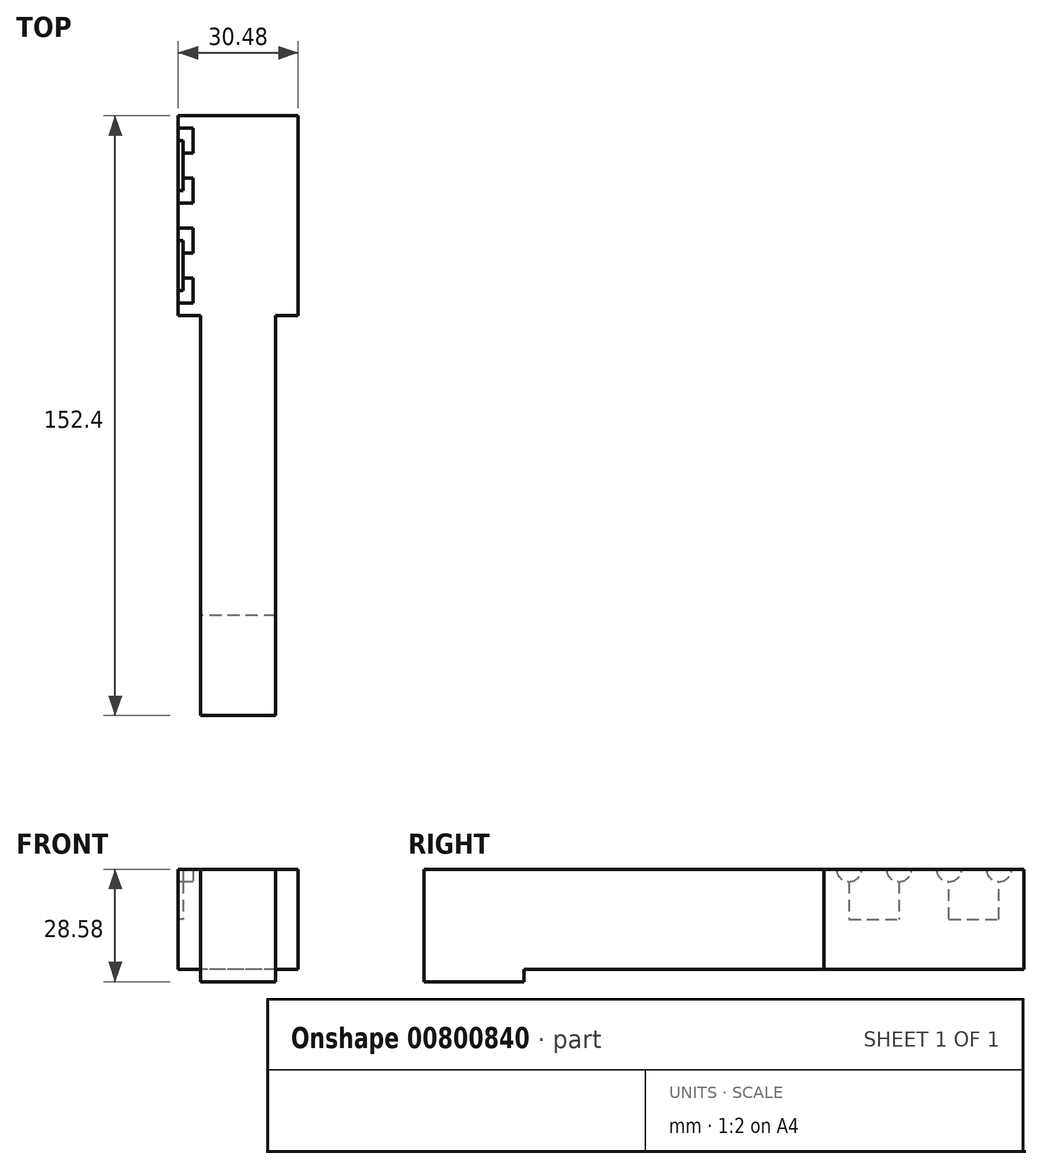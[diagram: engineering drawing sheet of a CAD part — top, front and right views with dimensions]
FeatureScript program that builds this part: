
annotation { "Feature Type Name" : "Feature", "Feature Type Description" : "" }
export const myFeature = defineFeature(function(context is Context, id is Id, definition is map)
    precondition{}
    {
        {
            var Q0;
            Q0=qCreatedBy(makeId("Right.planeOp"),FACE);
            var sketch = newSketch(context, id + "F0", { "sketchPlane" : qUnion([Q0])});
            skLineSegment(sketch, "E0", {"start": v(0, 0) * mm, "end": v(50.8, 0) * mm});
            skLineSegment(sketch, "E1", {"start": v(0, 0) * mm, "end": v(-76.2, 0) * mm});
            skLineSegment(sketch, "E2", {"start": v(50.8, 0) * mm, "end": v(50.8, 25.4) * mm});
            skLineSegment(sketch, "E3", {"start": v(50.8, 25.4) * mm, "end": v(0, 25.4) * mm});
            skLineSegment(sketch, "E4", {"start": v(0, 25.4) * mm, "end": v(0, 0) * mm});
            skLineSegment(sketch, "E5", {"start": v(-76.2, 0) * mm, "end": v(-76.2, 31.75) * mm});
            skLineSegment(sketch, "E6", {"start": v(0, 25.4) * mm, "end": v(-76.2, 25.4) * mm});
            skLineSegment(sketch, "E7", {"start": v(-76.2, 25.4) * mm, "end": v(-101.6, 25.4) * mm});
            skLineSegment(sketch, "E8", {"start": v(-101.6, 25.4) * mm, "end": v(-101.6, -3.18) * mm});
            skLineSegment(sketch, "E9", {"start": v(-101.6, -3.18) * mm, "end": v(-76.2, -3.18) * mm});
            skLineSegment(sketch, "E10", {"start": v(-76.2, -3.18) * mm, "end": v(-76.2, 0) * mm});
            skSolve(sketch);
        }
        {
            var Q0;
            {var subQ0=sQuery(id+"F0.wireOp",EDGE,"E1");Q0=makeQuery(id+"F0.imprint","IMPRINT",FACE,{"disambiguationData":[TD([[makeQuery(id+"F0.imprint","IMPRINT",EDGE,{"derivedFrom":subQ0}),-1.0]])]});}
            var Q1;
            {var subQ0=sQuery(id+"F0.wireOp",EDGE,"E7");Q1=makeQuery(id+"F0.imprint","IMPRINT",FACE,{"disambiguationData":[TD([[makeQuery(id+"F0.imprint","IMPRINT",EDGE,{"derivedFrom":subQ0}),1.0]])]});}
            extrude(context, id + "F1", {"entities" : qUnion([Q0, Q1]), "depth" : 9.52 * mm, "offsetDistance" : 25.4 * mm});
        }
        {
            var Q0;
            Q0=makeQuery(id+"F0.imprint","IMPRINT",FACE,{"disambiguationData":[TD([[makeQuery(id+"F0.imprint","IMPRINT",EDGE,{"derivedFrom":sQuery(id+"F0.wireOp",EDGE,"E0")}),1.0]])]});
            extrude(context, id + "F2", {"entities" : qUnion([Q0]), "operationType" : NewBodyOperationType.ADD, "depth" : 15.24 * mm, "offsetDistance" : 25.4 * mm});
        }
        {
            var Q0;
            Q0=makeQuery(id+"F0.imprint","IMPRINT",FACE,{"disambiguationData":[TD([[makeQuery(id+"F0.imprint","IMPRINT",EDGE,{"derivedFrom":sQuery(id+"F0.wireOp",EDGE,"E0")}),1.0]])]});
            extrude(context, id + "F3", {"entities" : qUnion([Q0]), "operationType" : NewBodyOperationType.ADD, "depth" : -15.24 * mm, "offsetDistance" : 25.4 * mm});
        }
        {
            var Q0;
            {var subQ0=sQuery(id+"F0.wireOp",EDGE,"E1");Q0=makeQuery(id+"F0.imprint","IMPRINT",FACE,{"disambiguationData":[TD([[makeQuery(id+"F0.imprint","IMPRINT",EDGE,{"derivedFrom":subQ0}),-1.0]])]});}
            var Q1;
            {var subQ0=sQuery(id+"F0.wireOp",EDGE,"E7");Q1=makeQuery(id+"F0.imprint","IMPRINT",FACE,{"disambiguationData":[TD([[makeQuery(id+"F0.imprint","IMPRINT",EDGE,{"derivedFrom":subQ0}),1.0]])]});}
            extrude(context, id + "F4", {"entities" : qUnion([Q0, Q1]), "operationType" : NewBodyOperationType.ADD, "depth" : -9.52 * mm, "offsetDistance" : 25.4 * mm});
        }
        {
            var Q0;
            Q0=makeQuery(id+"F3.opExtrude","CAP_FACE",FACE,{"disambiguationData":[OSD([sQuery(id+"F0.wireOp",EDGE,"E0"),sQuery(id+"F0.wireOp",EDGE,"E2"),sQuery(id+"F0.wireOp",EDGE,"E3"),sQuery(id+"F0.wireOp",EDGE,"E4")])],"isStart":false});
            var sketch = newSketch(context, id + "F5", { "sketchPlane" : qUnion([Q0])});
            skLineSegment(sketch, "E11", {"start": v(0, 12.7) * mm, "end": v(-50.8, 12.7) * mm});
            skLineSegment(sketch, "E12", {"start": v(0, 12.7) * mm, "end": v(0, 6.35) * mm});
            skLineSegment(sketch, "E13", {"start": v(0, 6.35) * mm, "end": v(-50.8, 6.35) * mm});
            skLineSegment(sketch, "E14", {"start": v(-25.4, 25.4) * mm, "end": v(-25.4, 12.7) * mm});
            skLineSegment(sketch, "E15", {"start": v(0, 25.4) * mm, "end": v(-12.7, 25.4) * mm});
            skLineSegment(sketch, "E16", {"start": v(-50.8, 25.4) * mm, "end": v(-38.1, 25.4) * mm});
            skLineSegment(sketch, "E17", {"start": v(-38.1, 25.4) * mm, "end": v(-38.1, 12.7) * mm});
            skLineSegment(sketch, "E18", {"start": v(-38.1, 12.7) * mm, "end": v(-44.45, 12.7) * mm});
            skLineSegment(sketch, "E19", {"start": v(-44.45, 12.7) * mm, "end": v(-31.75, 12.7) * mm});
            skLineSegment(sketch, "E20", {"start": v(-31.75, 12.7) * mm, "end": v(-31.75, 25.4) * mm});
            skLineSegment(sketch, "E21", {"start": v(-44.45, 12.7) * mm, "end": v(-44.45, 25.4) * mm});
            skLineSegment(sketch, "E22", {"start": v(-12.7, 25.4) * mm, "end": v(-12.7, 12.7) * mm});
            skLineSegment(sketch, "E23", {"start": v(-6.35, 25.4) * mm, "end": v(-6.35, 12.7) * mm});
            skLineSegment(sketch, "E24", {"start": v(-12.7, 25.4) * mm, "end": v(-25.4, 25.4) * mm});
            skLineSegment(sketch, "E25", {"start": v(-19.05, 25.4) * mm, "end": v(-19.05, 12.7) * mm});
            skArc(sketch, "E26", {"start": v(-28.57, 25.4) * mm, "mid": v(-31.75, 22.23) * mm, "end": v(-34.92, 25.4) * mm});
            skArc(sketch, "E27", {"start": v(-41.28, 25.4) * mm, "mid": v(-44.45, 22.23) * mm, "end": v(-47.62, 25.4) * mm});
            skArc(sketch, "E28", {"start": v(-3.18, 25.4) * mm, "mid": v(-6.35, 22.23) * mm, "end": v(-9.53, 25.4) * mm});
            skArc(sketch, "E29", {"start": v(-15.88, 25.4) * mm, "mid": v(-19.05, 22.23) * mm, "end": v(-22.23, 25.4) * mm});
            skLineSegment(sketch, "E30", {"start": v(-44.45, 12.7) * mm, "end": v(-47.62, 12.7) * mm});
            skLineSegment(sketch, "E31", {"start": v(-47.62, 12.7) * mm, "end": v(-47.62, 6.35) * mm});
            skLineSegment(sketch, "E32", {"start": v(-25.4, 12.7) * mm, "end": v(-25.4, 6.35) * mm});
            skLineSegment(sketch, "E33", {"start": v(-6.35, 12.7) * mm, "end": v(-3.18, 12.7) * mm});
            skLineSegment(sketch, "E34", {"start": v(-3.18, 12.7) * mm, "end": v(-3.18, 6.35) * mm});
            skLineSegment(sketch, "E35", {"start": v(-47.62, 6.35) * mm, "end": v(-46.1, 6.35) * mm});
            skLineSegment(sketch, "E36", {"start": v(-46.1, 6.35) * mm, "end": v(-46.1, 12.7) * mm});
            skLineSegment(sketch, "E37", {"start": v(-47.62, 6.35) * mm, "end": v(-49.15, 6.35) * mm});
            skLineSegment(sketch, "E38", {"start": v(-49.15, 6.35) * mm, "end": v(-49.15, 12.7) * mm});
            skLineSegment(sketch, "E39", {"start": v(-47.62, 12.7) * mm, "end": v(-47.62, 15.24) * mm});
            skLineSegment(sketch, "E40", {"start": v(-25.4, 6.35) * mm, "end": v(-27.94, 6.35) * mm});
            skLineSegment(sketch, "E41", {"start": v(-27.94, 6.35) * mm, "end": v(-27.94, 16.5) * mm});
            skLineSegment(sketch, "E42", {"start": v(-27.94, 16.5) * mm, "end": v(-22.86, 16.5) * mm});
            skLineSegment(sketch, "E43", {"start": v(-22.86, 16.5) * mm, "end": v(-22.86, 6.35) * mm});
            skLineSegment(sketch, "E44", {"start": v(-22.86, 6.35) * mm, "end": v(-25.4, 6.35) * mm});
            skLineSegment(sketch, "E45", {"start": v(-25.4, 16.5) * mm, "end": v(-25.4, 20.57) * mm});
            skLineSegment(sketch, "E46", {"start": v(-3.18, 6.35) * mm, "end": v(-1.65, 6.35) * mm});
            skLineSegment(sketch, "E47", {"start": v(-3.18, 6.35) * mm, "end": v(-4.7, 6.35) * mm});
            skLineSegment(sketch, "E48", {"start": v(-4.7, 6.35) * mm, "end": v(-4.7, 12.7) * mm});
            skLineSegment(sketch, "E49", {"start": v(-1.65, 6.35) * mm, "end": v(-1.65, 12.7) * mm});
            skLineSegment(sketch, "E50", {"start": v(-3.18, 12.7) * mm, "end": v(-3.18, 15.24) * mm});
            skArc(sketch, "E51", {"start": v(-47.62, 15.24) * mm, "mid": v(-48.75, 14.19) * mm, "end": v(-49.15, 12.7) * mm});
            skArc(sketch, "E52", {"start": v(-46.1, 12.7) * mm, "mid": v(-46.51, 14.18) * mm, "end": v(-47.63, 15.24) * mm});
            skArc(sketch, "E53", {"start": v(-25.4, 20.57) * mm, "mid": v(-27.27, 18.92) * mm, "end": v(-27.94, 16.5) * mm});
            skArc(sketch, "E54", {"start": v(-22.86, 16.5) * mm, "mid": v(-23.53, 18.92) * mm, "end": v(-25.4, 20.57) * mm});
            skArc(sketch, "E55", {"start": v(-1.65, 12.7) * mm, "mid": v(-2.05, 14.19) * mm, "end": v(-3.18, 15.24) * mm});
            skArc(sketch, "E56", {"start": v(-3.18, 15.24) * mm, "mid": v(-4.3, 14.19) * mm, "end": v(-4.7, 12.7) * mm});
            skLineSegment(sketch, "E57", {"start": v(-46.1, 6.35) * mm, "end": v(-42.47, 6.35) * mm});
            skLineSegment(sketch, "E58", {"start": v(-42.47, 6.35) * mm, "end": v(-38.84, 6.35) * mm});
            skLineSegment(sketch, "E59", {"start": v(-38.84, 6.35) * mm, "end": v(-35.2, 6.35) * mm});
            skLineSegment(sketch, "E60", {"start": v(-35.2, 6.35) * mm, "end": v(-31.57, 6.35) * mm});
            skLineSegment(sketch, "E61", {"start": v(-31.57, 6.35) * mm, "end": v(-27.94, 6.35) * mm});
            skLineSegment(sketch, "E62", {"start": v(-31.57, 6.35) * mm, "end": v(-31.57, 12.7) * mm});
            skLineSegment(sketch, "E63", {"start": v(-35.2, 6.35) * mm, "end": v(-35.2, 12.7) * mm});
            skLineSegment(sketch, "E64", {"start": v(-38.84, 6.35) * mm, "end": v(-38.84, 12.7) * mm});
            skLineSegment(sketch, "E65", {"start": v(-42.47, 6.35) * mm, "end": v(-42.47, 12.7) * mm});
            skLineSegment(sketch, "E66", {"start": v(-37.02, 6.35) * mm, "end": v(-37.02, 11.42) * mm});
            skLineSegment(sketch, "E67", {"start": v(-37.02, 6.35) * mm, "end": v(-37.02, 9.53) * mm});
            skLineSegment(sketch, "E68", {"start": v(-37.02, 9.53) * mm, "end": v(-36, 9.53) * mm});
            skLineSegment(sketch, "E69", {"start": v(-36, 9.53) * mm, "end": v(-36, 6.35) * mm});
            skLineSegment(sketch, "E70", {"start": v(-50.8, 6.35) * mm, "end": v(-38.84, 6.35) * mm});
            skLineSegment(sketch, "E71", {"start": v(-35.2, 6.35) * mm, "end": v(-38.84, 6.35) * mm});
            skLineSegment(sketch, "E72", {"start": v(-35.2, 12.7) * mm, "end": v(-38.84, 12.7) * mm});
            skLineSegment(sketch, "E73", {"start": v(-38.84, 6.35) * mm, "end": v(-37.02, 6.35) * mm});
            skLineSegment(sketch, "E74", {"start": v(-50.8, 6.35) * mm, "end": v(0, 6.35) * mm});
            skSolve(sketch);
        }
        {
            var Q0;
            {var subQ1=sQuery(id+"F5.wireOp",EDGE,"E17");Q0=makeQuery(id+"F5.imprint","IMPRINT",FACE,{"disambiguationData":[TD([[makeQuery(id+"F5.imprint","IMPRINT",EDGE,{"derivedFrom":subQ1}),-1.0]])]});}
            var Q1;
            {var subQ7=sQuery(id+"F5.wireOp",EDGE,"E17");Q1=makeQuery(id+"F5.imprint","IMPRINT",FACE,{"disambiguationData":[TD([[makeQuery(id+"F5.imprint","IMPRINT",EDGE,{"derivedFrom":subQ7}),1.0]])]});}
            var Q2;
            {var subQ1=sQuery(id+"F5.wireOp",EDGE,"E22");Q2=makeQuery(id+"F5.imprint","IMPRINT",FACE,{"disambiguationData":[TD([[makeQuery(id+"F5.imprint","IMPRINT",EDGE,{"derivedFrom":subQ1}),-1.0]])]});}
            var Q3;
            {var subQ0=sQuery(id+"F5.wireOp",EDGE,"E22");Q3=makeQuery(id+"F5.imprint","IMPRINT",FACE,{"disambiguationData":[TD([[makeQuery(id+"F5.imprint","IMPRINT",EDGE,{"derivedFrom":subQ0}),1.0]])]});}
            extrude(context, id + "F6", {"entities" : qUnion([Q0, Q1, Q2, Q3]), "operationType" : NewBodyOperationType.REMOVE, "oppositeDirection" : true, "depth" : 1.27 * mm, "offsetDistance" : 25.4 * mm});
        }
        {
            var Q0;
            {var subQ0=sQuery(id+"F5.wireOp",EDGE,"E21");var subQ1=sQuery(id+"F5.wireOp",EDGE,"E16");var subQ2=makeQuery(id+"F5.imprint","INTERSECT",VERTEX,{"derivedFrom":[subQ1,subQ0]});Q0=makeQuery(id+"F5.imprint","IMPRINT",FACE,{"disambiguationData":[TD([[makeQuery(id+"F5.imprint","IMPRINT",EDGE,{"disambiguationData":[TD([[subQ2,-1.0]])],"derivedFrom":subQ1}),-1.0]])]});}
            var Q1;
            {var subQ0=sQuery(id+"F5.wireOp",EDGE,"E21");var subQ1=sQuery(id+"F5.wireOp",EDGE,"E16");var subQ2=makeQuery(id+"F5.imprint","INTERSECT",VERTEX,{"derivedFrom":[subQ1,subQ0]});Q1=makeQuery(id+"F5.imprint","IMPRINT",FACE,{"disambiguationData":[TD([[makeQuery(id+"F5.imprint","IMPRINT",EDGE,{"disambiguationData":[TD([[subQ2,1.0]])],"derivedFrom":subQ1}),-1.0]])]});}
            var Q2;
            {var subQ0=sQuery(id+"F5.wireOp",EDGE,"E20");var subQ1=makeQuery(id+"F3.opExtrude","CAP_EDGE",EDGE,{"disambiguationData":[OSD([sQuery(id+"F0.wireOp",EDGE,"E3")])],"isStart":false});var subQ2=makeQuery(id+"F5.imprint","INTERSECT",VERTEX,{"derivedFrom":[subQ1,subQ0]});Q2=makeQuery(id+"F5.imprint","IMPRINT",FACE,{"disambiguationData":[TD([[makeQuery(id+"F5.imprint","IMPRINT",EDGE,{"disambiguationData":[TD([[subQ2,1.0]])],"derivedFrom":subQ0}),1.0]])]});}
            var Q3;
            {var subQ0=sQuery(id+"F5.wireOp",EDGE,"E20");var subQ1=makeQuery(id+"F3.opExtrude","CAP_EDGE",EDGE,{"disambiguationData":[OSD([sQuery(id+"F0.wireOp",EDGE,"E3")])],"isStart":false});var subQ2=makeQuery(id+"F5.imprint","INTERSECT",VERTEX,{"derivedFrom":[subQ1,subQ0]});Q3=makeQuery(id+"F5.imprint","IMPRINT",FACE,{"disambiguationData":[TD([[makeQuery(id+"F5.imprint","IMPRINT",EDGE,{"disambiguationData":[TD([[subQ2,1.0]])],"derivedFrom":subQ0}),-1.0]])]});}
            var Q4;
            {var subQ0=sQuery(id+"F5.wireOp",EDGE,"E25");var subQ1=sQuery(id+"F5.wireOp",EDGE,"E24");var subQ2=makeQuery(id+"F5.imprint","INTERSECT",VERTEX,{"derivedFrom":[subQ1,subQ0]});Q4=makeQuery(id+"F5.imprint","IMPRINT",FACE,{"disambiguationData":[TD([[makeQuery(id+"F5.imprint","IMPRINT",EDGE,{"disambiguationData":[TD([[subQ2,1.0]])],"derivedFrom":subQ1}),-1.0]])]});}
            var Q5;
            {var subQ0=sQuery(id+"F5.wireOp",EDGE,"E25");var subQ1=sQuery(id+"F5.wireOp",EDGE,"E24");var subQ2=makeQuery(id+"F5.imprint","INTERSECT",VERTEX,{"derivedFrom":[subQ1,subQ0]});Q5=makeQuery(id+"F5.imprint","IMPRINT",FACE,{"disambiguationData":[TD([[makeQuery(id+"F5.imprint","IMPRINT",EDGE,{"disambiguationData":[TD([[subQ2,-1.0]])],"derivedFrom":subQ1}),-1.0]])]});}
            var Q6;
            {var subQ0=sQuery(id+"F5.wireOp",EDGE,"E23");var subQ1=sQuery(id+"F5.wireOp",EDGE,"E15");var subQ2=makeQuery(id+"F5.imprint","INTERSECT",VERTEX,{"derivedFrom":[subQ1,subQ0]});Q6=makeQuery(id+"F5.imprint","IMPRINT",FACE,{"disambiguationData":[TD([[makeQuery(id+"F5.imprint","IMPRINT",EDGE,{"disambiguationData":[TD([[subQ2,1.0]])],"derivedFrom":subQ1}),-1.0]])]});}
            var Q7;
            {var subQ0=sQuery(id+"F5.wireOp",EDGE,"E23");var subQ1=sQuery(id+"F5.wireOp",EDGE,"E15");var subQ2=makeQuery(id+"F5.imprint","INTERSECT",VERTEX,{"derivedFrom":[subQ1,subQ0]});Q7=makeQuery(id+"F5.imprint","IMPRINT",FACE,{"disambiguationData":[TD([[makeQuery(id+"F5.imprint","IMPRINT",EDGE,{"disambiguationData":[TD([[subQ2,-1.0]])],"derivedFrom":subQ1}),-1.0]])]});}
            extrude(context, id + "F7", {"entities" : qUnion([Q0, Q1, Q2, Q3, Q4, Q5, Q6, Q7]), "operationType" : NewBodyOperationType.REMOVE, "oppositeDirection" : true, "depth" : 3.8 * mm, "offsetDistance" : 25.4 * mm});
        }
    });
